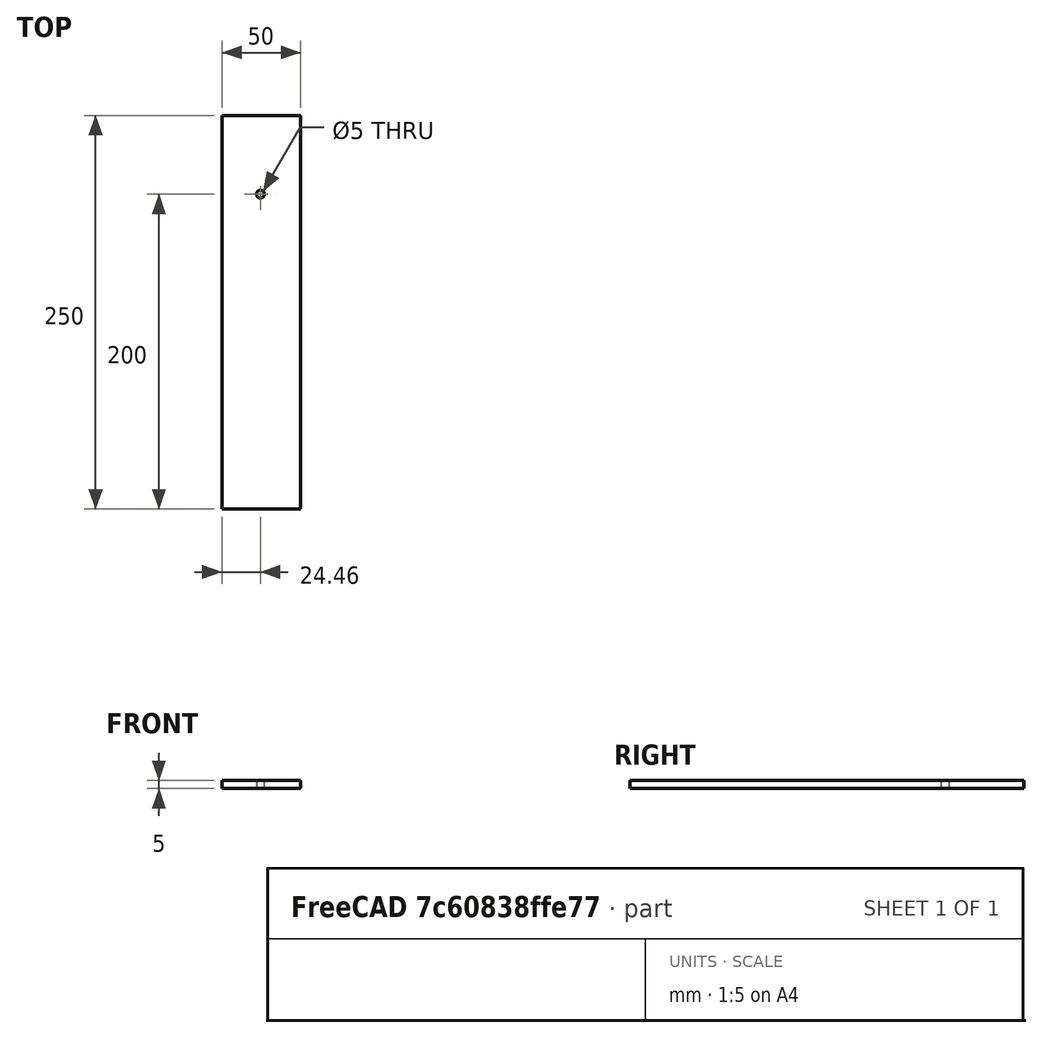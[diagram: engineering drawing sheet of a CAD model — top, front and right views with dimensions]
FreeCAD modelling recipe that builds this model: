
FCSTD DOCUMENT  (FreeCAD 0.19R24276 (Git))
Label: Osnovanie
License: All rights reserved
LicenseURL: http://en.wikipedia.org/wiki/All_rights_reserved
objects: Sketcher::SketchObject×1, PartDesign::Pad×1, PartDesign::Body×1
note: 4 computed .brp shape members not serialized (recipe doc carries the construction recipe); baked Part::Feature solids carry a one-line shape summary decoded from their .brp

FEATURE [Sketcher::SketchObject] Sketch
  FullyConstrained = false
  MapMode = 5
  Support = -> [XY_Plane]
  sketch-geometry (5):
    g0: LineSegment StartX=25.5407 StartY=-58.7601 StartZ=0 EndX=-24.4593 EndY=-58.7601 EndZ=0
    g1: LineSegment StartX=-24.4593 StartY=-58.7601 StartZ=0 EndX=-24.4593 EndY=191.24 EndZ=0
    g2: LineSegment StartX=-24.4593 StartY=191.24 StartZ=0 EndX=25.5407 EndY=191.24 EndZ=0
    g3: LineSegment StartX=25.5407 StartY=191.24 StartZ=0 EndX=25.5407 EndY=-58.7601 EndZ=0
    g4: Circle CenterX=0 CenterY=141.24 CenterZ=0 NormalX=0 NormalY=0 NormalZ=1 AngleXU=0 Radius=2.5
  constraints (13):
    c: Coincident(g0,g1)
    c: Coincident(g1,g2)
    c: Coincident(g2,g3)
    c: Coincident(g3,g0)
    c: Horizontal(g0)
    c: Horizontal(g2)
    c: Vertical(g1)
    c: Vertical(g3)
    c: DistanceY(g3,g3) = 250
    c: DistanceX(g2,g2) = 50
    c: PointOnObject(g4,g-2)
    c: Diameter(g4) = 5
    c: DistanceY(g0,g4) = 200
FEATURE [PartDesign::Pad] Pad
  Direction = (1,1,1)
  Length = 5
  Length2 = 100
  Profile = -> Sketch
  Type = 0
FEATURE [PartDesign::Body] Body  label="Body_osnovanie"
  Group = -> [Sketch,Pad]
  Origin = -> Origin
  Tip = -> Pad
